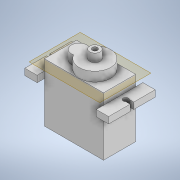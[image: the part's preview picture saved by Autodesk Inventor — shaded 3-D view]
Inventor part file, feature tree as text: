
AUTODESK INVENTOR PART (.ipt)
format: ipt  version: 2021.1 (Build 251245010, 245A)  size: 183,296 bytes
history: native  units: in
note: dims shown in document units (in); Inventor stores cm internally (conversion verified against a paired STEP export)
features: extrude x6, sketch x6, plane x5, mirror x2
ambient origin geometry x8: Origin, YZ Plane, XZ Plane, XY Plane, X Axis, Y Axis, Z Axis, Center Point
bodies: Solid1 (feature_tree)
feature tree (19):
  extrude  "Extrusion1"  Depth=0.4921in
  plane  "Work Plane3"
  plane  "Work Plane4"
  plane  "Work Plane5"
  extrude  "Extrusion2"  Depth=0.8937in
  mirror  "Mirror1"
  plane  "Work Plane6"
  extrude  "Extrusion3"  Depth=0.1102in
  extrude  "Extrusion4"  Depth=0.1102in
  extrude  "Extrusion5"  Depth=0.189in
  extrude  "Extrusion6"  Depth=0.0787in
  mirror  "Mirror2"
  sketch  "Sketch1"  dims[d0=0.9055in d1=0.4921in]
  plane  "Work Plane2"
  sketch  "Sketch2"  dims[d2=0.8937in d3=0.0in d4=0.4528in d5=-0.9055in d6=0.1969in d7=0.2461in]
  sketch  "Sketch3"  dims[d8=0.6299in d9=0.1102in]
  sketch  "Sketch4"  dims[d10=0.0984in d11=0.1102in]
  sketch  "Sketch5"  dims[d12=0.189in d13=0.0in d14=0.4331in]
  sketch  "Sketch6"  dims[d15=0.4173in d16=0.4803in d17=0.0787in d18=0.1575in d19=0.0in d20=0.1575in d21=0.126in d22=0.0in d23=0.126in d24=0.0in d25=0.0787in d26=0.0984in d27=0.0in d28=0.0787in]
